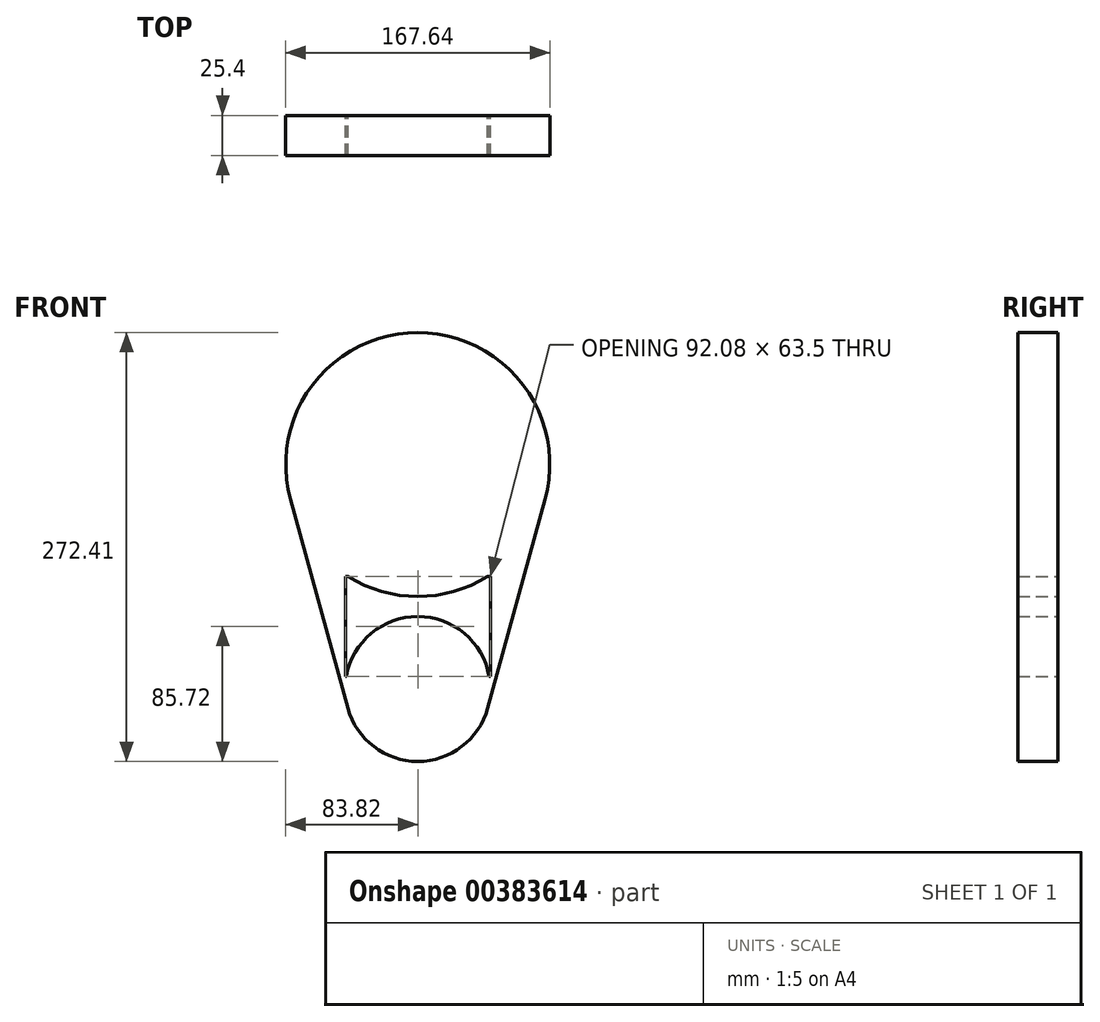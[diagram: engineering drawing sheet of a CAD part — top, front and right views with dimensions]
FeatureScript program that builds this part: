
annotation { "Feature Type Name" : "Feature", "Feature Type Description" : "" }
export const myFeature = defineFeature(function(context is Context, id is Id, definition is map)
    precondition{}
    {
        {
            var Q0;
            Q0=qCreatedBy(makeId("Front.planeOp"),FACE);
            var sketch = newSketch(context, id + "F0", { "sketchPlane" : qUnion([Q0])});
            skLineSegment(sketch, "E0.bottom", {"start": v(46.04, 31.75) * mm, "end": v(44.36, 31.75) * mm});
            skLineSegment(sketch, "E0.top", {"start": v(46.04, -31.75) * mm, "end": v(45.35, -31.75) * mm});
            skLineSegment(sketch, "E0.left", {"start": v(46.04, 31.75) * mm, "end": v(46.04, -31.75) * mm});
            skLineSegment(sketch, "E0.right", {"start": v(-46.04, 31.75) * mm, "end": v(-46.04, -31.75) * mm});
            skPoint(sketch, "E0.middle", {"position": v(0, 0) * mm});
            skPoint(sketch, "E1.endSnap0", {"position": v(0, 31.75) * mm});
            skArc(sketch, "E2", {"start": v(-44.36, 31.75) * mm, "mid": v(0, 19.05) * mm, "end": v(44.36, 31.75) * mm});
            skPoint(sketch, "E3.endSnap0", {"position": v(0, -31.75) * mm});
            skArc(sketch, "E4", {"start": v(45.35, -31.75) * mm, "mid": v(0, 6.35) * mm, "end": v(-45.35, -31.75) * mm});
            skLineSegment(sketch, "E5.trimOffspring", {"start": v(-44.36, 31.75) * mm, "end": v(-46.04, 31.75) * mm});
            skPoint(sketch, "E1.end.orphan", {"position": v(0, 19.05) * mm});
            skPoint(sketch, "E1.start.orphan", {"position": v(0, 31.75) * mm});
            skPoint(sketch, "E3.end.orphan", {"position": v(0, 6.35) * mm});
            skLineSegment(sketch, "E6.trimOffspring", {"start": v(-45.35, -31.75) * mm, "end": v(-46.04, -31.75) * mm});
            skArc(sketch, "E7", {"start": v(80.82, 80.65) * mm, "mid": v(0, 186.7) * mm, "end": v(-80.82, 80.65) * mm});
            skArc(sketch, "E8", {"start": v(-44.4, -51.89) * mm, "mid": v(0, -85.73) * mm, "end": v(44.4, -51.89) * mm});
            skLineSegment(sketch, "E9", {"start": v(-80.82, 80.65) * mm, "end": v(-44.4, -51.89) * mm});
            skLineSegment(sketch, "E10", {"start": v(44.4, -51.89) * mm, "end": v(80.82, 80.65) * mm});
            skPoint(sketch, "E11.orphan", {"position": v(0, -213.4) * mm});
            skSolve(sketch);
        }
        {
            var Q0;
            Q0 = qSketchRegion(id + "F0", true);
            extrude(context, id + "F1", {"entities" : qUnion([Q0]), "depth" : 25.4 * mm});
        }
    });
